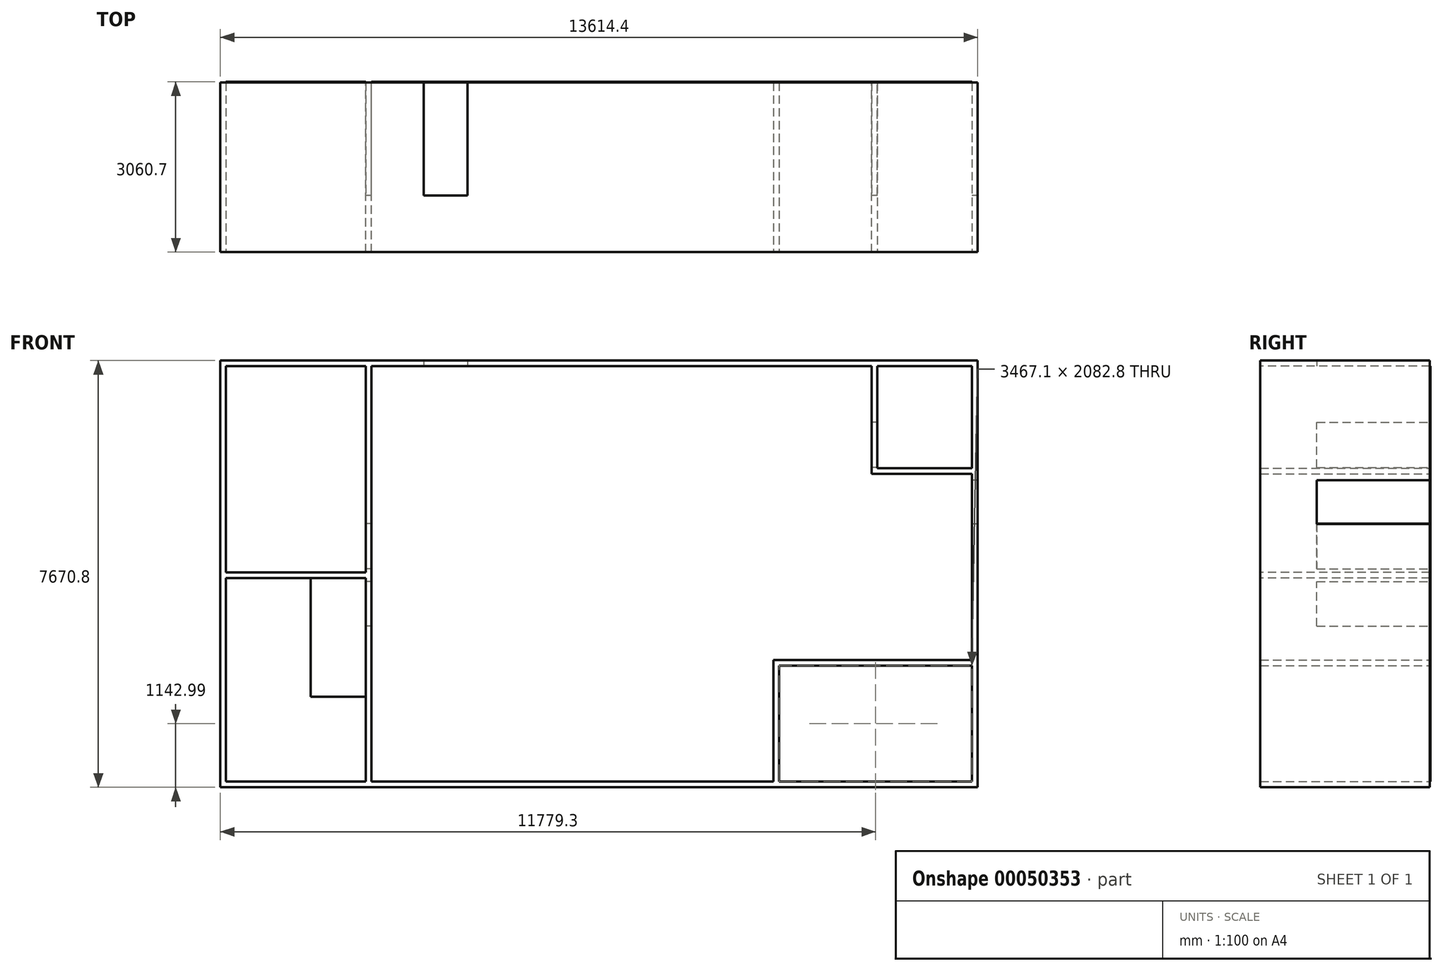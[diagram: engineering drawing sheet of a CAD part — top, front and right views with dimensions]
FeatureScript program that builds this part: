
annotation { "Feature Type Name" : "Feature", "Feature Type Description" : "" }
export const myFeature = defineFeature(function(context is Context, id is Id, definition is map)
    precondition{}
    {
        {
            var Q0;
            Q0=qCreatedBy(makeId("Front.planeOp"),FACE);
            var sketch = newSketch(context, id + "F0", { "sketchPlane" : qUnion([Q0])});
            skLineSegment(sketch, "E0.top", {"start": v(-11665.42, -4162.61) * mm, "end": v(-2673.82, -4162.61) * mm});
            skLineSegment(sketch, "E0.left", {"start": v(-11665.42, 3304.99) * mm, "end": v(-11665.42, -4162.61) * mm});
            skLineSegment(sketch, "E1.trimOffspring", {"start": v(-11665.42, 3304.99) * mm, "end": v(-2673.82, 3304.99) * mm});
            skLineSegment(sketch, "E2.trimOffspring", {"start": v(-2673.82, 3304.99) * mm, "end": v(-2673.82, -4162.61) * mm});
            skLineSegment(sketch, "E3.0", {"start": v(-11767.02, 3406.59) * mm, "end": v(-2572.22, 3406.59) * mm});
            skLineSegment(sketch, "E4.0", {"start": v(-2572.22, 3406.59) * mm, "end": v(-2572.22, -4264.21) * mm});
            skLineSegment(sketch, "E5.0", {"start": v(-11767.02, -4264.21) * mm, "end": v(-2572.22, -4264.21) * mm});
            skLineSegment(sketch, "E6.0", {"start": v(-11767.02, 3406.59) * mm, "end": v(-11767.02, -4264.21) * mm});
            skSolve(sketch);
        }
        {
            var Q0;
            Q0 = qSketchRegion(id + "F0", true);
            extrude(context, id + "F1", {"entities" : qUnion([Q0]), "depth" : 3048 * mm});
        }
        {
            var Q0;
            Q0=makeQuery(id+"F1.opExtrude","SWEPT_FACE",FACE,{"disambiguationData":[OSD([sQuery(id+"F0.wireOp",EDGE,"E4.0")])]});
            var sketch = newSketch(context, id + "F2", { "sketchPlane" : qUnion([Q0])});
            skLineSegment(sketch, "E7.bottom", {"start": v(0, 3406.59) * mm, "end": v(-3048, 3406.59) * mm});
            skLineSegment(sketch, "E7.top", {"start": v(0, 3304.99) * mm, "end": v(-3048, 3304.99) * mm});
            skLineSegment(sketch, "E7.left", {"start": v(0, 3406.59) * mm, "end": v(0, 3304.99) * mm});
            skLineSegment(sketch, "E7.right", {"start": v(-3048, 3406.59) * mm, "end": v(-3048, 3304.99) * mm});
            skLineSegment(sketch, "E8.bottom", {"start": v(-3048, 1469.84) * mm, "end": v(0, 1469.84) * mm});
            skLineSegment(sketch, "E8.top", {"start": v(-3048, 1368.24) * mm, "end": v(0, 1368.24) * mm});
            skLineSegment(sketch, "E8.left", {"start": v(-3048, 1469.84) * mm, "end": v(-3048, 1368.24) * mm});
            skLineSegment(sketch, "E8.right", {"start": v(0, 1469.84) * mm, "end": v(0, 1368.24) * mm});
            skSolve(sketch);
        }
        {
            var Q0;
            Q0 = qSketchRegion(id + "F2", true);
            extrude(context, id + "F3", {"entities" : qUnion([Q0]), "operationType" : NewBodyOperationType.ADD, "depth" : 1701.8 * mm});
        }
        {
            var Q0;
            {var subQ0=sQuery(id+"F0.wireOp",EDGE,"E5.0");var subQ2=sQuery(id+"F0.wireOp",EDGE,"E4.0");Q0=makeQuery(id+"F3.boolean.opBoolean","SPLIT",FACE,{"disambiguationData":[TD([makeQuery(id+"F1.opExtrude","SWEPT_FACE",FACE,{"disambiguationData":[OSD([subQ0])]})])],"derivedFrom":makeQuery(id+"F1.opExtrude","SWEPT_FACE",FACE,{"disambiguationData":[OSD([subQ2])]})});}
            var sketch = newSketch(context, id + "F4", { "sketchPlane" : qUnion([Q0])});
            skLineSegment(sketch, "E9.bottom", {"start": v(0, 1368.24) * mm, "end": v(-3048, 1368.24) * mm});
            skLineSegment(sketch, "E9.top", {"start": v(0, -4162.61) * mm, "end": v(-3048, -4162.61) * mm});
            skLineSegment(sketch, "E9.left", {"start": v(0, 1368.24) * mm, "end": v(0, -4162.61) * mm});
            skLineSegment(sketch, "E9.right", {"start": v(-3048, 1368.24) * mm, "end": v(-3048, -4162.61) * mm});
            skSolve(sketch);
        }
        {
            var Q0;
            Q0 = qSketchRegion(id + "F4", true);
            extrude(context, id + "F5", {"entities" : qUnion([Q0]), "operationType" : NewBodyOperationType.REMOVE, "oppositeDirection" : true, "depth" : 2336.8 * mm});
        }
        {
            var Q0;
            Q0=makeQuery(id+"F3.boolean.opBoolean","MERGE",FACE,{"derivedFrom":[makeQuery(id+"F1.opExtrude","SWEPT_FACE",FACE,{"disambiguationData":[OSD([sQuery(id+"F0.wireOp",EDGE,"E3.0")])]}),makeQuery(id+"F3.opExtrude","SWEPT_FACE",FACE,{"disambiguationData":[OSD([sQuery(id+"F2.wireOp",EDGE,"E7.bottom")])]})]});
            var sketch = newSketch(context, id + "F6", { "sketchPlane" : qUnion([Q0])});
            skLineSegment(sketch, "E10.bottom", {"start": v(-870.42, 0) * mm, "end": v(-768.82, 0) * mm});
            skLineSegment(sketch, "E10.top", {"start": v(-870.42, -3048) * mm, "end": v(-768.82, -3048) * mm});
            skLineSegment(sketch, "E10.left", {"start": v(-870.42, 0) * mm, "end": v(-870.42, -3048) * mm});
            skLineSegment(sketch, "E10.right", {"start": v(-768.82, 0) * mm, "end": v(-768.82, -3048) * mm});
            skSolve(sketch);
        }
        {
            var Q0;
            Q0 = qSketchRegion(id + "F6", true);
            var Q1;
            Q1=makeQuery(id+"F1.opExtrude","SWEPT_FACE",FACE,{"disambiguationData":[OSD([sQuery(id+"F0.wireOp",EDGE,"E5.0")])]});
            extrude(context, id + "F7", {"entities" : qUnion([Q0]), "operationType" : NewBodyOperationType.ADD, "endBound" : BoundingType.UP_TO_SURFACE, "oppositeDirection" : true, "endBoundEntityFace" : qUnion([Q1]), "depth" : 7721.6 * mm});
        }
        {
            var Q0;
            {var subQ0=sQuery(id+"F0.wireOp",EDGE,"E5.0");var subQ2=sQuery(id+"F0.wireOp",EDGE,"E4.0");Q0=makeQuery(id+"F3.boolean.opBoolean","SPLIT",FACE,{"disambiguationData":[TD([makeQuery(id+"F1.opExtrude","SWEPT_FACE",FACE,{"disambiguationData":[OSD([subQ0])]})])],"derivedFrom":makeQuery(id+"F1.opExtrude","SWEPT_FACE",FACE,{"disambiguationData":[OSD([subQ2])]})});}
            var sketch = newSketch(context, id + "F8", { "sketchPlane" : qUnion([Q0])});
            skLineSegment(sketch, "E11.bottom", {"start": v(-3048, -4264.21) * mm, "end": v(0, -4264.21) * mm});
            skLineSegment(sketch, "E11.top", {"start": v(-3048, -4162.61) * mm, "end": v(0, -4162.61) * mm});
            skLineSegment(sketch, "E11.left", {"start": v(-3048, -4264.21) * mm, "end": v(-3048, -4162.61) * mm});
            skLineSegment(sketch, "E11.right", {"start": v(0, -4264.21) * mm, "end": v(0, -4162.61) * mm});
            skSolve(sketch);
        }
        {
            var Q0;
            Q0 = qSketchRegion(id + "F8", true);
            extrude(context, id + "F9", {"entities" : qUnion([Q0]), "operationType" : NewBodyOperationType.ADD, "endBound" : BoundingType.UP_TO_NEXT, "depth" : 2016.76 * mm});
        }
        {
            var Q0;
            Q0=makeQuery(id+"F7.boolean.opBoolean","SPLIT",FACE,{"disambiguationData":[TD([makeQuery(id+"F3.opExtrude","SWEPT_FACE",FACE,{"disambiguationData":[OSD([sQuery(id+"F2.wireOp",EDGE,"E8.top")])]})])],"derivedFrom":makeQuery(id+"F7.opExtrude","SWEPT_FACE",FACE,{"disambiguationData":[OSD([sQuery(id+"F6.wireOp",EDGE,"E10.left")])]})});
            var sketch = newSketch(context, id + "F10", { "sketchPlane" : qUnion([Q0])});
            skLineSegment(sketch, "E12.bottom", {"start": v(3048, -1978.21) * mm, "end": v(0, -1978.21) * mm});
            skLineSegment(sketch, "E12.top", {"start": v(3048, -2079.81) * mm, "end": v(0, -2079.81) * mm});
            skLineSegment(sketch, "E12.left", {"start": v(3048, -1978.21) * mm, "end": v(3048, -2079.81) * mm});
            skLineSegment(sketch, "E12.right", {"start": v(0, -1978.21) * mm, "end": v(0, -2079.81) * mm});
            skSolve(sketch);
        }
        {
            var Q0;
            Q0 = qSketchRegion(id + "F10", true);
            extrude(context, id + "F11", {"entities" : qUnion([Q0]), "operationType" : NewBodyOperationType.ADD, "depth" : 3568.7 * mm});
        }
        {
            var Q0;
            Q0=makeQuery(id+"F11.opExtrude","SWEPT_FACE",FACE,{"disambiguationData":[OSD([sQuery(id+"F10.wireOp",EDGE,"E12.top")])]});
            var sketch = newSketch(context, id + "F12", { "sketchPlane" : qUnion([Q0])});
            skLineSegment(sketch, "E13.bottom", {"start": v(-4439.12, 3048) * mm, "end": v(-4337.52, 3048) * mm});
            skLineSegment(sketch, "E13.top", {"start": v(-4439.12, 0) * mm, "end": v(-4337.52, 0) * mm});
            skLineSegment(sketch, "E13.left", {"start": v(-4439.12, 3048) * mm, "end": v(-4439.12, 0) * mm});
            skLineSegment(sketch, "E13.right", {"start": v(-4337.52, 3048) * mm, "end": v(-4337.52, 0) * mm});
            skSolve(sketch);
        }
        {
            var Q0;
            Q0 = qSketchRegion(id + "F12", true);
            extrude(context, id + "F13", {"entities" : qUnion([Q0]), "operationType" : NewBodyOperationType.ADD, "endBound" : BoundingType.UP_TO_NEXT, "depth" : 25.4 * mm});
        }
        {
            var Q0;
            Q0=makeQuery(id+"F1.opExtrude","SWEPT_FACE",FACE,{"disambiguationData":[OSD([sQuery(id+"F0.wireOp",EDGE,"E6.0")])]});
            var sketch = newSketch(context, id + "F14", { "sketchPlane" : qUnion([Q0])});
            skLineSegment(sketch, "E14.bottom", {"start": v(0, 3406.59) * mm, "end": v(3048, 3406.59) * mm});
            skLineSegment(sketch, "E14.top", {"start": v(0, 3304.99) * mm, "end": v(3048, 3304.99) * mm});
            skLineSegment(sketch, "E14.left", {"start": v(0, 3406.59) * mm, "end": v(0, 3304.99) * mm});
            skLineSegment(sketch, "E14.right", {"start": v(3048, 3406.59) * mm, "end": v(3048, 3304.99) * mm});
            skLineSegment(sketch, "E15.bottom", {"start": v(3048, -4264.21) * mm, "end": v(0, -4264.21) * mm});
            skLineSegment(sketch, "E15.top", {"start": v(3048, -4162.61) * mm, "end": v(0, -4162.61) * mm});
            skLineSegment(sketch, "E15.left", {"start": v(3048, -4264.21) * mm, "end": v(3048, -4162.61) * mm});
            skLineSegment(sketch, "E15.right", {"start": v(0, -4264.21) * mm, "end": v(0, -4162.61) * mm});
            skLineSegment(sketch, "E16.bottom", {"start": v(0, -403.41) * mm, "end": v(3048, -403.41) * mm});
            skLineSegment(sketch, "E16.top", {"start": v(0, -505.01) * mm, "end": v(3048, -505.01) * mm});
            skLineSegment(sketch, "E16.left", {"start": v(0, -403.41) * mm, "end": v(0, -505.01) * mm});
            skLineSegment(sketch, "E16.right", {"start": v(3048, -403.41) * mm, "end": v(3048, -505.01) * mm});
            skSolve(sketch);
        }
        {
            var Q0;
            Q0 = qSketchRegion(id + "F14", true);
            extrude(context, id + "F15", {"entities" : qUnion([Q0]), "operationType" : NewBodyOperationType.ADD, "depth" : 2514.6 * mm});
        }
        {
            var Q0;
            {var subQ0=sQuery(id+"F0.wireOp",EDGE,"E5.0");Q0=makeQuery(id+"F15.boolean.opBoolean","MERGE",FACE,{"derivedFrom":[makeQuery(id+"F9.boolean.opBoolean","MERGE",FACE,{"derivedFrom":[makeQuery(id+"F1.opExtrude","SWEPT_FACE",FACE,{"disambiguationData":[OSD([subQ0])]}),makeQuery(id+"F7.opExtrude","CAP_FACE",FACE,{"disambiguationData":[OSD([subQ0])],"isStart":false}),makeQuery(id+"F9.opExtrude","SWEPT_FACE",FACE,{"disambiguationData":[OSD([sQuery(id+"F8.wireOp",EDGE,"E11.bottom")])]})]}),makeQuery(id+"F15.opExtrude","SWEPT_FACE",FACE,{"disambiguationData":[OSD([sQuery(id+"F14.wireOp",EDGE,"E15.bottom")])]})]});}
            var sketch = newSketch(context, id + "F16", { "sketchPlane" : qUnion([Q0])});
            skLineSegment(sketch, "E17.bottom", {"start": v(-14281.62, 0) * mm, "end": v(-14383.22, 0) * mm});
            skLineSegment(sketch, "E17.top", {"start": v(-14281.62, 3048) * mm, "end": v(-14383.22, 3048) * mm});
            skLineSegment(sketch, "E17.left", {"start": v(-14281.62, 0) * mm, "end": v(-14281.62, 3048) * mm});
            skLineSegment(sketch, "E17.right", {"start": v(-14383.22, 0) * mm, "end": v(-14383.22, 3048) * mm});
            skSolve(sketch);
        }
        {
            var Q0;
            Q0 = qSketchRegion(id + "F16", true);
            var Q1;
            Q1=makeQuery(id+"F15.boolean.opBoolean","MERGE",FACE,{"derivedFrom":[makeQuery(id+"F7.boolean.opBoolean","MERGE",FACE,{"derivedFrom":[makeQuery(id+"F3.boolean.opBoolean","MERGE",FACE,{"derivedFrom":[makeQuery(id+"F1.opExtrude","SWEPT_FACE",FACE,{"disambiguationData":[OSD([sQuery(id+"F0.wireOp",EDGE,"E3.0")])]}),makeQuery(id+"F3.opExtrude","SWEPT_FACE",FACE,{"disambiguationData":[OSD([sQuery(id+"F2.wireOp",EDGE,"E7.bottom")])]})]}),makeQuery(id+"F7.opExtrude","CAP_FACE",FACE,{"disambiguationData":[OSD([sQuery(id+"F6.wireOp",EDGE,"E10.bottom"),sQuery(id+"F6.wireOp",EDGE,"E10.top"),sQuery(id+"F6.wireOp",EDGE,"E10.left"),sQuery(id+"F6.wireOp",EDGE,"E10.right")])],"isStart":true})]}),makeQuery(id+"F15.opExtrude","SWEPT_FACE",FACE,{"disambiguationData":[OSD([sQuery(id+"F14.wireOp",EDGE,"E14.bottom")])]})]});
            extrude(context, id + "F17", {"entities" : qUnion([Q0]), "operationType" : NewBodyOperationType.ADD, "endBound" : BoundingType.UP_TO_SURFACE, "oppositeDirection" : true, "endBoundEntityFace" : qUnion([Q1]), "depth" : 25.4 * mm});
        }
        {
            var Q0;
            Q0=makeQuery(id+"F1.opExtrude","SWEPT_FACE",FACE,{"disambiguationData":[OSD([sQuery(id+"F0.wireOp",EDGE,"E1.trimOffspring")])]});
            var sketch = newSketch(context, id + "F18", { "sketchPlane" : qUnion([Q0])});
            skLineSegment(sketch, "E18.bottom", {"start": v(-10725.62, 0) * mm, "end": v(-9938.22, 0) * mm});
            skLineSegment(sketch, "E18.top", {"start": v(-10725.62, 2032) * mm, "end": v(-9938.22, 2032) * mm});
            skLineSegment(sketch, "E18.left", {"start": v(-10725.62, 0) * mm, "end": v(-10725.62, 2032) * mm});
            skLineSegment(sketch, "E18.right", {"start": v(-9938.22, 0) * mm, "end": v(-9938.22, 2032) * mm});
            skSolve(sketch);
        }
        {
            var Q0;
            Q0 = qSketchRegion(id + "F18", true);
            extrude(context, id + "F19", {"entities" : qUnion([Q0]), "operationType" : NewBodyOperationType.REMOVE, "oppositeDirection" : true, "depth" : 5664.2 * mm});
        }
        {
            var Q0;
            {var subQ0=sQuery(id+"F0.wireOp",EDGE,"E6.0");Q0=makeQuery(id+"F15.boolean.opBoolean","SPLIT",FACE,{"disambiguationData":[TD([makeQuery(id+"F15.opExtrude","SWEPT_FACE",FACE,{"disambiguationData":[OSD([sQuery(id+"F14.wireOp",EDGE,"E14.top")])]})])],"derivedFrom":makeQuery(id+"F1.opExtrude","SWEPT_FACE",FACE,{"disambiguationData":[OSD([subQ0])]})});}
            var sketch = newSketch(context, id + "F20", { "sketchPlane" : qUnion([Q0])});
            skLineSegment(sketch, "E19.bottom", {"start": v(0, 472.89) * mm, "end": v(2032, 472.89) * mm});
            skLineSegment(sketch, "E19.top", {"start": v(0, -339.91) * mm, "end": v(2032, -339.91) * mm});
            skLineSegment(sketch, "E19.left", {"start": v(0, 472.89) * mm, "end": v(0, -339.91) * mm});
            skLineSegment(sketch, "E19.right", {"start": v(2032, 472.89) * mm, "end": v(2032, -339.91) * mm});
            skLineSegment(sketch, "E20.bottom", {"start": v(0, -568.51) * mm, "end": v(2032, -568.51) * mm});
            skLineSegment(sketch, "E20.top", {"start": v(0, -1368.61) * mm, "end": v(2032, -1368.61) * mm});
            skLineSegment(sketch, "E20.left", {"start": v(0, -568.51) * mm, "end": v(0, -1368.61) * mm});
            skLineSegment(sketch, "E20.right", {"start": v(2032, -568.51) * mm, "end": v(2032, -1368.61) * mm});
            skSolve(sketch);
        }
        {
            var Q0;
            Q0 = qSketchRegion(id + "F20", true);
            extrude(context, id + "F21", {"entities" : qUnion([Q0]), "operationType" : NewBodyOperationType.REMOVE, "oppositeDirection" : true, "depth" : 2133.6 * mm});
        }
        {
            var Q0;
            Q0=makeQuery(id+"F1.opExtrude","SWEPT_FACE",FACE,{"disambiguationData":[OSD([sQuery(id+"F0.wireOp",EDGE,"E2.trimOffspring")])]});
            var sketch = newSketch(context, id + "F22", { "sketchPlane" : qUnion([Q0])});
            skLineSegment(sketch, "E21.bottom", {"start": v(0, 2295.34) * mm, "end": v(2032, 2295.34) * mm});
            skLineSegment(sketch, "E21.top", {"start": v(0, 1482.54) * mm, "end": v(2032, 1482.54) * mm});
            skLineSegment(sketch, "E21.left", {"start": v(0, 2295.34) * mm, "end": v(0, 1482.54) * mm});
            skLineSegment(sketch, "E21.right", {"start": v(2032, 2295.34) * mm, "end": v(2032, 1482.54) * mm});
            skSolve(sketch);
        }
        {
            var Q0;
            Q0 = qSketchRegion(id + "F22", true);
            extrude(context, id + "F23", {"entities" : qUnion([Q0]), "operationType" : NewBodyOperationType.REMOVE, "oppositeDirection" : true, "depth" : 355.6 * mm});
        }
        {
            var Q0;
            {var subQ4=makeQuery(id+"F3.opExtrude","SWEPT_FACE",FACE,{"disambiguationData":[OSD([sQuery(id+"F2.wireOp",EDGE,"E8.top")])]});Q0=makeQuery(id+"F11.boolean.opBoolean","SPLIT",FACE,{"disambiguationData":[TD([subQ4])],"derivedFrom":makeQuery(id+"F7.boolean.opBoolean","SPLIT",FACE,{"disambiguationData":[TD([subQ4])],"derivedFrom":makeQuery(id+"F7.opExtrude","SWEPT_FACE",FACE,{"disambiguationData":[OSD([sQuery(id+"F6.wireOp",EDGE,"E10.left")])]})})});}
            var sketch = newSketch(context, id + "F24", { "sketchPlane" : qUnion([Q0])});
            skLineSegment(sketch, "E22.bottom", {"start": v(0, 1253.94) * mm, "end": v(2032, 1253.94) * mm});
            skLineSegment(sketch, "E22.top", {"start": v(0, 466.54) * mm, "end": v(2032, 466.54) * mm});
            skLineSegment(sketch, "E22.left", {"start": v(0, 1253.94) * mm, "end": v(0, 466.54) * mm});
            skLineSegment(sketch, "E22.right", {"start": v(2032, 1253.94) * mm, "end": v(2032, 466.54) * mm});
            skSolve(sketch);
        }
        {
            var Q0;
            Q0 = qSketchRegion(id + "F24", true);
            extrude(context, id + "F25", {"entities" : qUnion([Q0]), "operationType" : NewBodyOperationType.REMOVE, "oppositeDirection" : true, "depth" : 2870.2 * mm});
        }
        {
            var Q0;
            {var subQ3=sQuery(id+"F6.wireOp",EDGE,"E10.bottom");var subQ4=sQuery(id+"F0.wireOp",EDGE,"E2.trimOffspring");var subQ5=sQuery(id+"F0.wireOp",EDGE,"E4.0");var subQ6=sQuery(id+"F0.wireOp",EDGE,"E1.trimOffspring");var subQ9=sQuery(id+"F0.wireOp",EDGE,"E3.0");Q0=makeQuery(id+"F25.boolean.opBoolean","SPLIT",FACE,{"disambiguationData":[TD([makeQuery(id+"F1.opExtrude","SWEPT_FACE",FACE,{"disambiguationData":[OSD([subQ4])]})])],"derivedFrom":makeQuery(id+"F17.boolean.opBoolean","MERGE",FACE,{"derivedFrom":[makeQuery(id+"F15.boolean.opBoolean","MERGE",FACE,{"derivedFrom":[makeQuery(id+"F13.boolean.opBoolean","MERGE",FACE,{"derivedFrom":[makeQuery(id+"F11.boolean.opBoolean","MERGE",FACE,{"derivedFrom":[makeQuery(id+"F9.boolean.opBoolean","MERGE",FACE,{"derivedFrom":[makeQuery(id+"F7.boolean.opBoolean","MERGE",FACE,{"derivedFrom":[makeQuery(id+"F3.boolean.opBoolean","MERGE",FACE,{"derivedFrom":[makeQuery(id+"F1.opExtrude","CAP_FACE",FACE,{"disambiguationData":[OSD([sQuery(id+"F0.wireOp",EDGE,"E0.top"),sQuery(id+"F0.wireOp",EDGE,"E0.left"),subQ6,subQ4,subQ9,subQ5,sQuery(id+"F0.wireOp",EDGE,"E5.0"),sQuery(id+"F0.wireOp",EDGE,"E6.0")])],"isStart":true}),makeQuery(id+"F3.opExtrude","SWEPT_FACE",FACE,{"disambiguationData":[OSD([sQuery(id+"F2.wireOp",EDGE,"E7.left")])]}),makeQuery(id+"F3.opExtrude","SWEPT_FACE",FACE,{"disambiguationData":[OSD([sQuery(id+"F2.wireOp",EDGE,"E8.right")])]})]}),makeQuery(id+"F7.opExtrude","SWEPT_FACE",FACE,{"disambiguationData":[OSD([subQ3])]})]}),makeQuery(id+"F9.opExtrude","SWEPT_FACE",FACE,{"disambiguationData":[OSD([sQuery(id+"F8.wireOp",EDGE,"E11.right")])]})]}),makeQuery(id+"F11.opExtrude","SWEPT_FACE",FACE,{"disambiguationData":[OSD([sQuery(id+"F10.wireOp",EDGE,"E12.right")])]})]}),makeQuery(id+"F13.opExtrude","SWEPT_FACE",FACE,{"disambiguationData":[OSD([sQuery(id+"F12.wireOp",EDGE,"E13.top")])]})]}),makeQuery(id+"F15.opExtrude","SWEPT_FACE",FACE,{"disambiguationData":[OSD([sQuery(id+"F14.wireOp",EDGE,"E14.left")])]}),makeQuery(id+"F15.opExtrude","SWEPT_FACE",FACE,{"disambiguationData":[OSD([sQuery(id+"F14.wireOp",EDGE,"E15.right")])]}),makeQuery(id+"F15.opExtrude","SWEPT_FACE",FACE,{"disambiguationData":[OSD([sQuery(id+"F14.wireOp",EDGE,"E16.left")])]})]}),makeQuery(id+"F17.opExtrude","SWEPT_FACE",FACE,{"disambiguationData":[OSD([sQuery(id+"F16.wireOp",EDGE,"E17.bottom")])]})]})});}
            var sketch = newSketch(context, id + "F26", { "sketchPlane" : qUnion([Q0])});
            skLineSegment(sketch, "E23", {"start": v(3893.02, 3304.99) * mm, "end": v(3893.02, 1368.24) * mm});
            skLineSegment(sketch, "E24", {"start": v(3893.02, 1368.24) * mm, "end": v(9633.42, 1368.24) * mm});
            skLineSegment(sketch, "E25", {"start": v(9633.42, 1368.24) * mm, "end": v(9633.42, 3304.99) * mm});
            skLineSegment(sketch, "E26", {"start": v(9633.42, 3304.99) * mm, "end": v(11665.42, 3304.99) * mm});
            skLineSegment(sketch, "E27", {"start": v(11665.42, 3304.99) * mm, "end": v(11665.42, -1673.41) * mm});
            skLineSegment(sketch, "E28", {"start": v(11665.42, -1673.41) * mm, "end": v(10446.22, -1673.41) * mm});
            skLineSegment(sketch, "E29", {"start": v(10446.22, -1673.41) * mm, "end": v(10446.22, 149.04) * mm});
            skLineSegment(sketch, "E30", {"start": v(10446.22, 149.04) * mm, "end": v(870.42, 149.04) * mm});
            skLineSegment(sketch, "E31", {"start": v(3893.02, 3304.99) * mm, "end": v(2673.82, 3304.99) * mm});
            skLineSegment(sketch, "E32", {"start": v(2673.82, 3304.99) * mm, "end": v(2673.82, 1368.24) * mm});
            skLineSegment(sketch, "E33", {"start": v(2673.82, 1368.24) * mm, "end": v(870.42, 1368.24) * mm});
            skLineSegment(sketch, "E34", {"start": v(870.42, 1368.24) * mm, "end": v(870.42, 149.04) * mm});
            skSolve(sketch);
        }
        {
            var Q0;
            Q0 = qSketchRegion(id + "F26", true);
            extrude(context, id + "F27", {"entities" : qUnion([Q0]), "depth" : 12.7 * mm});
        }
        {
            var Q0;
            Q0=makeQuery(id+"F27.opExtrude","CAP_FACE",FACE,{"disambiguationData":[OSD([sQuery(id+"F26.wireOp",EDGE,"E23"),sQuery(id+"F26.wireOp",EDGE,"E24"),sQuery(id+"F26.wireOp",EDGE,"E25"),sQuery(id+"F26.wireOp",EDGE,"E26"),sQuery(id+"F26.wireOp",EDGE,"E27"),sQuery(id+"F26.wireOp",EDGE,"E28"),sQuery(id+"F26.wireOp",EDGE,"E29"),sQuery(id+"F26.wireOp",EDGE,"E30"),sQuery(id+"F26.wireOp",EDGE,"E31"),sQuery(id+"F26.wireOp",EDGE,"E32"),sQuery(id+"F26.wireOp",EDGE,"E33"),sQuery(id+"F26.wireOp",EDGE,"E34")])],"isStart":true});
            var sketch = newSketch(context, id + "F28", { "sketchPlane" : qUnion([Q0])});
            skLineSegment(sketch, "E35.bottom", {"start": v(-9633.42, 1368.24) * mm, "end": v(-6763.22, 1368.24) * mm});
            skLineSegment(sketch, "E35.top", {"start": v(-9633.42, 3304.99) * mm, "end": v(-6763.22, 3304.99) * mm});
            skLineSegment(sketch, "E35.left", {"start": v(-9633.42, 1368.24) * mm, "end": v(-9633.42, 3304.99) * mm});
            skLineSegment(sketch, "E35.right", {"start": v(-6763.22, 1368.24) * mm, "end": v(-6763.22, 3304.99) * mm});
            skSolve(sketch);
        }
        {
            var Q0;
            Q0 = qSketchRegion(id + "F28", true);
            var Q1;
            Q1=makeQuery(id+"F27.opExtrude","CAP_FACE",FACE,{"disambiguationData":[OSD([sQuery(id+"F26.wireOp",EDGE,"E23"),sQuery(id+"F26.wireOp",EDGE,"E24"),sQuery(id+"F26.wireOp",EDGE,"E25"),sQuery(id+"F26.wireOp",EDGE,"E26"),sQuery(id+"F26.wireOp",EDGE,"E27"),sQuery(id+"F26.wireOp",EDGE,"E28"),sQuery(id+"F26.wireOp",EDGE,"E29"),sQuery(id+"F26.wireOp",EDGE,"E30"),sQuery(id+"F26.wireOp",EDGE,"E31"),sQuery(id+"F26.wireOp",EDGE,"E32"),sQuery(id+"F26.wireOp",EDGE,"E33"),sQuery(id+"F26.wireOp",EDGE,"E34")])],"isStart":false});
            extrude(context, id + "F29", {"entities" : qUnion([Q0]), "endBound" : BoundingType.UP_TO_SURFACE, "oppositeDirection" : true, "endBoundEntityFace" : qUnion([Q1]), "depth" : 25.4 * mm});
        }
        {
            var Q0;
            Q0=makeQuery(id+"F27.opExtrude","CAP_FACE",FACE,{"disambiguationData":[OSD([sQuery(id+"F26.wireOp",EDGE,"E23"),sQuery(id+"F26.wireOp",EDGE,"E24"),sQuery(id+"F26.wireOp",EDGE,"E25"),sQuery(id+"F26.wireOp",EDGE,"E26"),sQuery(id+"F26.wireOp",EDGE,"E27"),sQuery(id+"F26.wireOp",EDGE,"E28"),sQuery(id+"F26.wireOp",EDGE,"E29"),sQuery(id+"F26.wireOp",EDGE,"E30"),sQuery(id+"F26.wireOp",EDGE,"E31"),sQuery(id+"F26.wireOp",EDGE,"E32"),sQuery(id+"F26.wireOp",EDGE,"E33"),sQuery(id+"F26.wireOp",EDGE,"E34")])],"isStart":true});
            var sketch = newSketch(context, id + "F30", { "sketchPlane" : qUnion([Q0])});
            skPoint(sketch, "E36.firstSnap0", {"position": v(-6763.22, 1368.24) * mm});
            skLineSegment(sketch, "E36.bottom", {"start": v(-6763.22, 1368.24) * mm, "end": v(-3893.02, 1368.24) * mm});
            skLineSegment(sketch, "E36.top", {"start": v(-6763.22, 3304.99) * mm, "end": v(-3893.02, 3304.99) * mm});
            skLineSegment(sketch, "E36.left", {"start": v(-6763.22, 1368.24) * mm, "end": v(-6763.22, 3304.99) * mm});
            skLineSegment(sketch, "E36.right", {"start": v(-3893.02, 1368.24) * mm, "end": v(-3893.02, 3304.99) * mm});
            skSolve(sketch);
        }
        {
            var Q0;
            Q0 = qSketchRegion(id + "F30", true);
            extrude(context, id + "F31", {"entities" : qUnion([Q0]), "oppositeDirection" : true, "depth" : 12.7 * mm});
        }
        {
            var Q0;
            Q0=makeQuery(id+"F27.opExtrude","CAP_FACE",FACE,{"disambiguationData":[OSD([sQuery(id+"F26.wireOp",EDGE,"E23"),sQuery(id+"F26.wireOp",EDGE,"E24"),sQuery(id+"F26.wireOp",EDGE,"E25"),sQuery(id+"F26.wireOp",EDGE,"E26"),sQuery(id+"F26.wireOp",EDGE,"E27"),sQuery(id+"F26.wireOp",EDGE,"E28"),sQuery(id+"F26.wireOp",EDGE,"E29"),sQuery(id+"F26.wireOp",EDGE,"E30"),sQuery(id+"F26.wireOp",EDGE,"E31"),sQuery(id+"F26.wireOp",EDGE,"E32"),sQuery(id+"F26.wireOp",EDGE,"E33"),sQuery(id+"F26.wireOp",EDGE,"E34")])],"isStart":true});
            var sketch = newSketch(context, id + "F32", { "sketchPlane" : qUnion([Q0])});
            skLineSegment(sketch, "E37.bottom", {"start": v(-870.42, 149.04) * mm, "end": v(-4439.12, 149.04) * mm});
            skLineSegment(sketch, "E37.top", {"start": v(-870.42, -1978.21) * mm, "end": v(-4439.12, -1978.21) * mm});
            skLineSegment(sketch, "E37.left", {"start": v(-870.42, 149.04) * mm, "end": v(-870.42, -1978.21) * mm});
            skLineSegment(sketch, "E37.right", {"start": v(-4439.12, 149.04) * mm, "end": v(-4439.12, -1978.21) * mm});
            skSolve(sketch);
        }
        {
            var Q0;
            Q0 = qSketchRegion(id + "F32", true);
            extrude(context, id + "F33", {"entities" : qUnion([Q0]), "oppositeDirection" : true, "depth" : 12.7 * mm});
        }
        {
            var Q0;
            Q0=makeQuery(id+"F27.opExtrude","CAP_FACE",FACE,{"disambiguationData":[OSD([sQuery(id+"F26.wireOp",EDGE,"E23"),sQuery(id+"F26.wireOp",EDGE,"E24"),sQuery(id+"F26.wireOp",EDGE,"E25"),sQuery(id+"F26.wireOp",EDGE,"E26"),sQuery(id+"F26.wireOp",EDGE,"E27"),sQuery(id+"F26.wireOp",EDGE,"E28"),sQuery(id+"F26.wireOp",EDGE,"E29"),sQuery(id+"F26.wireOp",EDGE,"E30"),sQuery(id+"F26.wireOp",EDGE,"E31"),sQuery(id+"F26.wireOp",EDGE,"E32"),sQuery(id+"F26.wireOp",EDGE,"E33"),sQuery(id+"F26.wireOp",EDGE,"E34")])],"isStart":true});
            var sketch = newSketch(context, id + "F34", { "sketchPlane" : qUnion([Q0])});
            skLineSegment(sketch, "E38.bottom", {"start": v(-14281.62, -2638.61) * mm, "end": v(-12757.62, -2638.61) * mm});
            skLineSegment(sketch, "E38.top", {"start": v(-14281.62, -505.01) * mm, "end": v(-12757.62, -505.01) * mm});
            skLineSegment(sketch, "E38.left", {"start": v(-14281.62, -2638.61) * mm, "end": v(-14281.62, -505.01) * mm});
            skLineSegment(sketch, "E38.right", {"start": v(-12757.62, -2638.61) * mm, "end": v(-12757.62, -505.01) * mm});
            skSolve(sketch);
        }
        {
            var Q0;
            Q0 = qSketchRegion(id + "F34", true);
            extrude(context, id + "F35", {"entities" : qUnion([Q0]), "oppositeDirection" : true, "depth" : 12.7 * mm});
        }
        {
            var Q0;
            Q0=makeQuery(id+"F35.opExtrude","CAP_FACE",FACE,{"disambiguationData":[OSD([sQuery(id+"F34.wireOp",EDGE,"E38.bottom"),sQuery(id+"F34.wireOp",EDGE,"E38.top"),sQuery(id+"F34.wireOp",EDGE,"E38.left"),sQuery(id+"F34.wireOp",EDGE,"E38.right")])],"isStart":true});
            var sketch = newSketch(context, id + "F36", { "sketchPlane" : qUnion([Q0])});
            skLineSegment(sketch, "E39.bottom", {"start": v(-14281.62, -2638.61) * mm, "end": v(-11767.02, -2638.61) * mm});
            skLineSegment(sketch, "E39.top", {"start": v(-14281.62, -4162.61) * mm, "end": v(-11767.02, -4162.61) * mm});
            skLineSegment(sketch, "E39.left", {"start": v(-14281.62, -2638.61) * mm, "end": v(-14281.62, -4162.61) * mm});
            skLineSegment(sketch, "E39.right", {"start": v(-11767.02, -2638.61) * mm, "end": v(-11767.02, -4162.61) * mm});
            skSolve(sketch);
        }
        {
            var Q0;
            Q0 = qSketchRegion(id + "F36", true);
            extrude(context, id + "F37", {"entities" : qUnion([Q0]), "operationType" : NewBodyOperationType.ADD, "oppositeDirection" : true, "depth" : 12.7 * mm});
        }
        {
            var Q0;
            Q0=makeQuery(id+"F33.opExtrude","CAP_FACE",FACE,{"disambiguationData":[OSD([sQuery(id+"F32.wireOp",EDGE,"E37.bottom"),sQuery(id+"F32.wireOp",EDGE,"E37.top"),sQuery(id+"F32.wireOp",EDGE,"E37.left"),sQuery(id+"F32.wireOp",EDGE,"E37.right")])],"isStart":true});
            var sketch = newSketch(context, id + "F38", { "sketchPlane" : qUnion([Q0])});
            skLineSegment(sketch, "E40.bottom", {"start": v(-6572.72, -809.81) * mm, "end": v(-4439.12, -809.81) * mm});
            skLineSegment(sketch, "E40.top", {"start": v(-6572.72, -4162.61) * mm, "end": v(-4439.12, -4162.61) * mm});
            skLineSegment(sketch, "E40.left", {"start": v(-6572.72, -809.81) * mm, "end": v(-6572.72, -4162.61) * mm});
            skLineSegment(sketch, "E40.right", {"start": v(-4439.12, -809.81) * mm, "end": v(-4439.12, -4162.61) * mm});
            skLineSegment(sketch, "E41.MirrorCS", {"start": v(-6572.72, -809.81) * mm, "end": v(-8706.32, -809.81) * mm});
            skLineSegment(sketch, "E42.MirrorCS", {"start": v(-8706.32, -809.81) * mm, "end": v(-8706.32, -4162.61) * mm});
            skLineSegment(sketch, "E43.MirrorCS", {"start": v(-6572.72, -4162.61) * mm, "end": v(-8706.32, -4162.61) * mm});
            skLineSegment(sketch, "E44.bottom", {"start": v(-8706.32, -4162.61) * mm, "end": v(-11665.42, -4162.61) * mm});
            skLineSegment(sketch, "E44.top", {"start": v(-8706.32, -1673.41) * mm, "end": v(-11665.42, -1673.41) * mm});
            skLineSegment(sketch, "E44.left", {"start": v(-8706.32, -4162.61) * mm, "end": v(-8706.32, -1673.41) * mm});
            skLineSegment(sketch, "E44.right", {"start": v(-11665.42, -4162.61) * mm, "end": v(-11665.42, -1673.41) * mm});
            skSolve(sketch);
        }
        {
            var Q0;
            Q0=makeQuery(id+"F38.imprint","IMPRINT",FACE,{"disambiguationData":[TD([[makeQuery(id+"F38.imprint","IMPRINT",EDGE,{"derivedFrom":sQuery(id+"F38.wireOp",EDGE,"E44.bottom")}),-1.0]])]});
            extrude(context, id + "F39", {"entities" : qUnion([Q0]), "oppositeDirection" : true, "depth" : 12.7 * mm});
        }
        {
            var Q0;
            Q0=makeQuery(id+"F38.imprint","IMPRINT",FACE,{"disambiguationData":[TD([[makeQuery(id+"F38.imprint","IMPRINT",EDGE,{"derivedFrom":sQuery(id+"F38.wireOp",EDGE,"E40.left")}),-1.0]])]});
            extrude(context, id + "F40", {"entities" : qUnion([Q0]), "oppositeDirection" : true, "depth" : 12.7 * mm});
        }
        {
            var Q0;
            {var subQ3=sQuery(id+"F38.wireOp",EDGE,"E40.bottom");Q0=makeQuery(id+"F38.imprint","IMPRINT",FACE,{"disambiguationData":[TD([[makeQuery(id+"F38.imprint","IMPRINT",EDGE,{"derivedFrom":subQ3}),-1.0]])]});}
            extrude(context, id + "F41", {"entities" : qUnion([Q0]), "operationType" : NewBodyOperationType.ADD, "oppositeDirection" : true, "depth" : 12.7 * mm});
        }
        {
            var Q0;
            Q0=makeQuery(id+"F27.opExtrude","CAP_FACE",FACE,{"disambiguationData":[OSD([sQuery(id+"F26.wireOp",EDGE,"E23"),sQuery(id+"F26.wireOp",EDGE,"E24"),sQuery(id+"F26.wireOp",EDGE,"E25"),sQuery(id+"F26.wireOp",EDGE,"E26"),sQuery(id+"F26.wireOp",EDGE,"E27"),sQuery(id+"F26.wireOp",EDGE,"E28"),sQuery(id+"F26.wireOp",EDGE,"E29"),sQuery(id+"F26.wireOp",EDGE,"E30"),sQuery(id+"F26.wireOp",EDGE,"E31"),sQuery(id+"F26.wireOp",EDGE,"E32"),sQuery(id+"F26.wireOp",EDGE,"E33"),sQuery(id+"F26.wireOp",EDGE,"E34")])],"isStart":true});
            var sketch = newSketch(context, id + "F42", { "sketchPlane" : qUnion([Q0])});
            skLineSegment(sketch, "E45.bottom", {"start": v(-4439.12, -809.81) * mm, "end": v(-10446.22, -809.81) * mm});
            skLineSegment(sketch, "E45.top", {"start": v(-4439.12, 149.04) * mm, "end": v(-10446.22, 149.04) * mm});
            skLineSegment(sketch, "E45.left", {"start": v(-4439.12, -809.81) * mm, "end": v(-4439.12, 149.04) * mm});
            skLineSegment(sketch, "E45.right", {"start": v(-10446.22, -809.81) * mm, "end": v(-10446.22, 149.04) * mm});
            skSolve(sketch);
        }
        {
            var Q0;
            Q0 = qSketchRegion(id + "F42", true);
            var Q1;
            Q1=makeQuery(id+"F27.opExtrude","CAP_FACE",FACE,{"disambiguationData":[OSD([sQuery(id+"F26.wireOp",EDGE,"E23"),sQuery(id+"F26.wireOp",EDGE,"E24"),sQuery(id+"F26.wireOp",EDGE,"E25"),sQuery(id+"F26.wireOp",EDGE,"E26"),sQuery(id+"F26.wireOp",EDGE,"E27"),sQuery(id+"F26.wireOp",EDGE,"E28"),sQuery(id+"F26.wireOp",EDGE,"E29"),sQuery(id+"F26.wireOp",EDGE,"E30"),sQuery(id+"F26.wireOp",EDGE,"E31"),sQuery(id+"F26.wireOp",EDGE,"E32"),sQuery(id+"F26.wireOp",EDGE,"E33"),sQuery(id+"F26.wireOp",EDGE,"E34")])],"isStart":true});
            var Q2;
            Q2=makeQuery(id+"F27.opExtrude","CAP_FACE",FACE,{"disambiguationData":[OSD([sQuery(id+"F26.wireOp",EDGE,"E23"),sQuery(id+"F26.wireOp",EDGE,"E24"),sQuery(id+"F26.wireOp",EDGE,"E25"),sQuery(id+"F26.wireOp",EDGE,"E26"),sQuery(id+"F26.wireOp",EDGE,"E27"),sQuery(id+"F26.wireOp",EDGE,"E28"),sQuery(id+"F26.wireOp",EDGE,"E29"),sQuery(id+"F26.wireOp",EDGE,"E30"),sQuery(id+"F26.wireOp",EDGE,"E31"),sQuery(id+"F26.wireOp",EDGE,"E32"),sQuery(id+"F26.wireOp",EDGE,"E33"),sQuery(id+"F26.wireOp",EDGE,"E34")])],"isStart":false});
            extrude(context, id + "F43", {"entities" : qUnion([Q0, Q1]), "operationType" : NewBodyOperationType.ADD, "endBound" : BoundingType.UP_TO_SURFACE, "oppositeDirection" : true, "endBoundEntityFace" : qUnion([Q2]), "depth" : 25.4 * mm});
        }
        {
            var Q0;
            {var subQ0=sQuery(id+"F26.wireOp",EDGE,"E34");var subQ1=sQuery(id+"F26.wireOp",EDGE,"E33");var subQ2=sQuery(id+"F26.wireOp",EDGE,"E32");var subQ3=sQuery(id+"F26.wireOp",EDGE,"E31");var subQ4=sQuery(id+"F26.wireOp",EDGE,"E30");var subQ5=sQuery(id+"F26.wireOp",EDGE,"E29");var subQ6=sQuery(id+"F26.wireOp",EDGE,"E28");var subQ7=sQuery(id+"F26.wireOp",EDGE,"E27");var subQ8=sQuery(id+"F26.wireOp",EDGE,"E26");var subQ9=sQuery(id+"F26.wireOp",EDGE,"E25");var subQ10=sQuery(id+"F26.wireOp",EDGE,"E24");var subQ11=sQuery(id+"F26.wireOp",EDGE,"E23");Q0=makeQuery(id+"F43.boolean.opBoolean","MERGE",FACE,{"derivedFrom":[makeQuery(id+"F27.opExtrude","CAP_FACE",FACE,{"disambiguationData":[OSD([subQ11,subQ10,subQ9,subQ8,subQ7,subQ6,subQ5,subQ4,subQ3,subQ2,subQ1,subQ0])],"isStart":true}),makeQuery(id+"F43.opExtrude","CAP_FACE",FACE,{"disambiguationData":[OSD([subQ11,subQ10,subQ9,subQ8,subQ7,subQ6,subQ5,subQ4,subQ3,subQ2,subQ1,subQ0])],"isStart":true}),makeQuery(id+"F43.opExtrude","CAP_FACE",FACE,{"disambiguationData":[OSD([sQuery(id+"F42.wireOp",EDGE,"E45.bottom"),sQuery(id+"F42.wireOp",EDGE,"E45.top"),sQuery(id+"F42.wireOp",EDGE,"E45.left"),sQuery(id+"F42.wireOp",EDGE,"E45.right")])],"isStart":true})]});}
            var sketch = newSketch(context, id + "F44", { "sketchPlane" : qUnion([Q0])});
            skLineSegment(sketch, "E46.bottom", {"start": v(-10446.22, -809.81) * mm, "end": v(-8706.32, -809.81) * mm});
            skLineSegment(sketch, "E46.top", {"start": v(-10446.22, -1673.41) * mm, "end": v(-8706.32, -1673.41) * mm});
            skLineSegment(sketch, "E46.left", {"start": v(-10446.22, -809.81) * mm, "end": v(-10446.22, -1673.41) * mm});
            skLineSegment(sketch, "E46.right", {"start": v(-8706.32, -809.81) * mm, "end": v(-8706.32, -1673.41) * mm});
            skSolve(sketch);
        }
        {
            var Q0;
            Q0 = qSketchRegion(id + "F44", true);
            var Q1;
            Q1=makeQuery(id+"F39.opExtrude","CAP_FACE",FACE,{"disambiguationData":[OSD([sQuery(id+"F38.wireOp",EDGE,"E44.bottom"),sQuery(id+"F38.wireOp",EDGE,"E44.top"),sQuery(id+"F38.wireOp",EDGE,"E44.left"),sQuery(id+"F38.wireOp",EDGE,"E44.right")])],"isStart":false});
            extrude(context, id + "F45", {"entities" : qUnion([Q0]), "operationType" : NewBodyOperationType.ADD, "endBound" : BoundingType.UP_TO_SURFACE, "oppositeDirection" : true, "endBoundEntityFace" : qUnion([Q1]), "depth" : 25.4 * mm});
        }
    });
